# Revit family: 4804-COto 62
name_source: partatom
category: Windows
revit_build: Autodesk Revit LT 2016 (Build: 20150220_1215(x64)
units: mm (PartAtom-declared; Revit-internal decimal feet)

## family parameters
Always vertical = Yes
Cut with Voids When Loaded = No
Host = Wall
OmniClass Number = 23.30.20.00
OmniClass Title = Windows
Room Calculation Point = No
Shared = No

## types (1)
- 1188x1788mm
    Default Sill Height = 800 mm
    Height = 1788 mm
    Joint = 12 mm  [stored 0.0393701 ft]
    Manufacturer = www.kronevinduer.dk
    Mullion 1 Placement = 594 mm  [stored 1.94882 ft]
    Mullion 2 Placement = 596 mm  [stored 1.95538 ft]
    Mullion 3 Placement = 1192 mm  [stored 3.91076 ft]
    Offset from wall = 40 mm  [stored 0.131234 ft]
    Rough Height = 1812 mm  [stored 5.94488 ft]
    Rough Width = 1212 mm
    Wall Closure = By host
    Width = 1188 mm  [stored 3.89764 ft]

note: [stored X ft] marks values corroborated as IEEE doubles in the binary element streams (Revit-internal decimal feet)

## geometry (parser evidence)
native form markers: Sweep x4
no freeform markers — native parametric forms only
